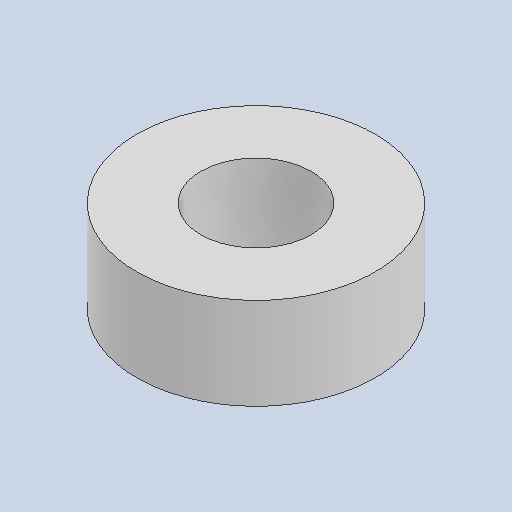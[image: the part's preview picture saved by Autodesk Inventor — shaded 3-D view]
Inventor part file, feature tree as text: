
AUTODESK INVENTOR PART (.ipt)
format: ipt  version: 2023 (Build 270158000, 158)  size: 133,632 bytes
history: native  units: in
note: dims shown in document units (in); Inventor stores cm internally (conversion verified against a paired STEP export)
features: extrude x1, sketch x1
ambient origin geometry x8: Origin, YZ Plane, XZ Plane, XY Plane, X Axis, Y Axis, Z Axis, Center Point
bodies: Solid1 (feature_tree)
feature tree (2):
  extrude  "Extrusion1"  Depth=0.1969in
  sketch  "Sketch1"  dims[d0=0.5118in d1=0.2362in d2=0.1969in d3=0.0in]
